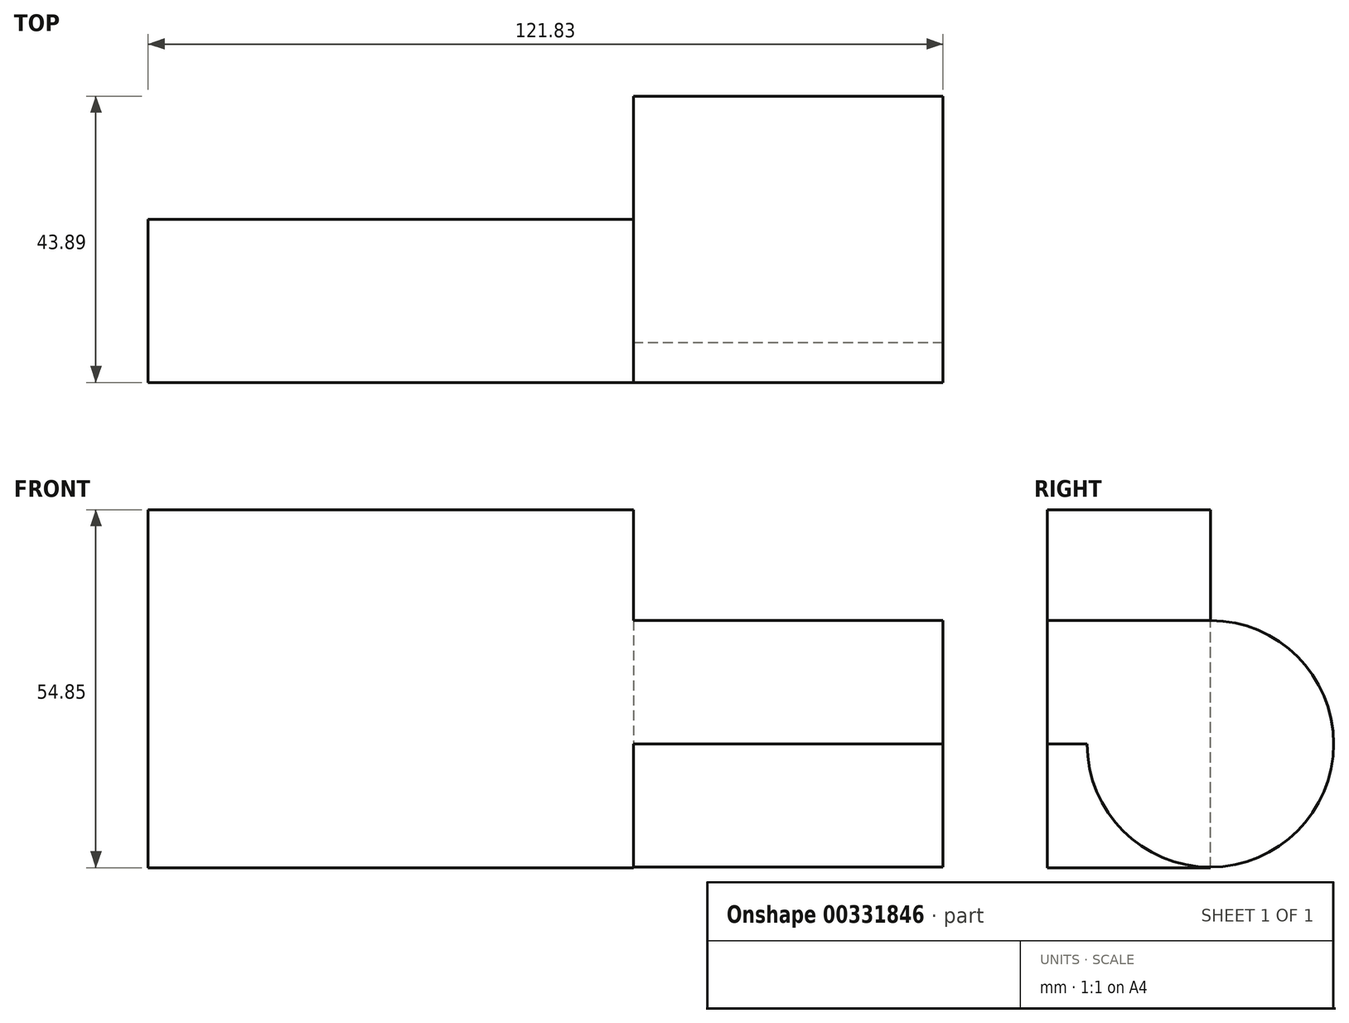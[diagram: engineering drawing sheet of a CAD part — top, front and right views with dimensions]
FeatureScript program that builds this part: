
annotation { "Feature Type Name" : "Feature", "Feature Type Description" : "" }
export const myFeature = defineFeature(function(context is Context, id is Id, definition is map)
    precondition{}
    {
        {
            var Q0;
            Q0=qCreatedBy(makeId("Front.planeOp"),FACE);
            var sketch = newSketch(context, id + "F0", { "sketchPlane" : qUnion([Q0])});
            skLineSegment(sketch, "E0.bottom", {"start": v(-74.41, 0) * mm, "end": v(0, 0) * mm});
            skLineSegment(sketch, "E0.top", {"start": v(-74.41, 54.85) * mm, "end": v(0, 54.85) * mm});
            skLineSegment(sketch, "E0.left", {"start": v(-74.41, 0) * mm, "end": v(-74.41, 54.85) * mm});
            skLineSegment(sketch, "E0.right", {"start": v(0, 0) * mm, "end": v(0, 54.85) * mm});
            skLineSegment(sketch, "E1", {"start": v(0, 18.99) * mm, "end": v(47.42, 18.99) * mm});
            skLineSegment(sketch, "E2", {"start": v(47.42, 18.99) * mm, "end": v(47.42, 37.88) * mm});
            skLineSegment(sketch, "E3", {"start": v(47.42, 37.88) * mm, "end": v(0, 37.88) * mm});
            skLineSegment(sketch, "E4", {"start": v(0, 37.88) * mm, "end": v(0, 18.99) * mm});
            skSolve(sketch);
        }
        {
            var Q0;
            Q0=makeQuery(id+"F0.imprint","IMPRINT",FACE,{"disambiguationData":[TD([[makeQuery(id+"F0.imprint","IMPRINT",EDGE,{"derivedFrom":sQuery(id+"F0.wireOp",EDGE,"E1")}),1.0]])]});
            var Q1;
            Q1=sQuery(id+"F0.wireOp",EDGE,"E1");
            revolve(context, id + "F1", {"entities" : qUnion([Q0]), "axis" : qUnion([Q1]), "revolveType" : RevolveType.FULL});
        }
        {
            var Q0;
            Q0 = qSketchRegion(id + "F0", true);
            extrude(context, id + "F2", {"entities" : qUnion([Q0]), "operationType" : NewBodyOperationType.ADD, "depth" : 25 * mm});
        }
    });
